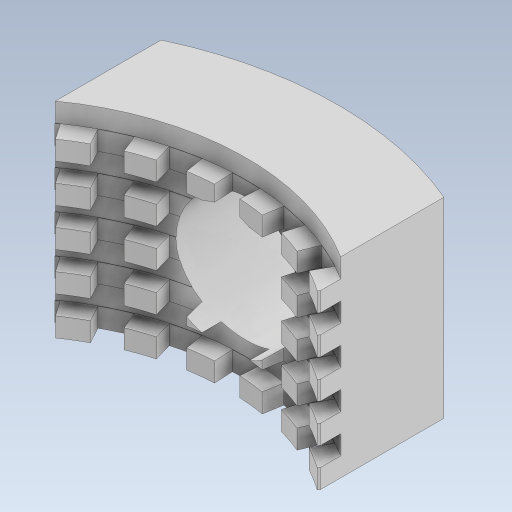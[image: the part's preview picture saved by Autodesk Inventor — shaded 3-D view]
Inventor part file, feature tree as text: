
AUTODESK INVENTOR PART (.ipt)
format: ipt  version: 2023 (Build 270158000, 158)  size: 547,840 bytes
history: native  units: in
note: dims shown in document units (in); Inventor stores cm internally (conversion verified against a paired STEP export)
features: sketch x7, extrude x6, revolve x1, plane x1, projected_geometry x1
ambient origin geometry x8: Origin, YZ Plane, XZ Plane, XY Plane, X Axis, Y Axis, Z Axis, Center Point
bodies: Solid1 (feature_tree)
feature tree (16):
  extrude  "Extrusion1"  Depth=0.2362in TaperAngle=0.0deg
  extrude  "Extrusion2"  Depth=0.3937in TaperAngle=0.0deg
  extrude  "Extrusion3"  Depth=0.0394in TaperAngle=120.0deg
  revolve  "Revolution1"  [1 undecoded]
  extrude  "Extrusion13"  Depth=0.2362in TaperAngle=0.0deg
  plane  "Work Plane5"
  extrude  "Extrusion14"  TaperAngle=0.0deg  [1 undecoded]
  extrude  "Extrusion15"  TaperAngle=0.0deg  [1 undecoded]
  sketch  "Sketch1"  dims[d0=1.0236in d1=0.2362in d2=0.0in]
  sketch  "Sketch2"  dims[d3=120.0deg d4=0.3937in d5=0.0in]
  sketch  "Sketch3"  dims[d6=0.0394in d7=7.874in d9=120.0deg]
  sketch  "Sketch4"  dims[d11=0.3937in d12=0.0in d14=3.937in d16=0.0394in d17=0.3937in d19=0.3937in]
  sketch  "Sketch25"  dims[d21=360.0deg d105=0.2362in d106=0.0in]
  projected_geometry  "Projected Loop9"
  sketch  "Sketch26"  dims[d107=0.2559in d108=0.0in d109=0.0in]
  sketch  "Sketch27"  dims[d110=0.5709in d111=0.0in d112=0.0in d91=0.0344in d92=0.0344in d93=0.0197in d94=0.0344in]
note: 3 required parameter values undecoded (feature->parameter linkage not recoverable at this tier; creation-order binding heuristic only, values carry confidence <= 0.55)